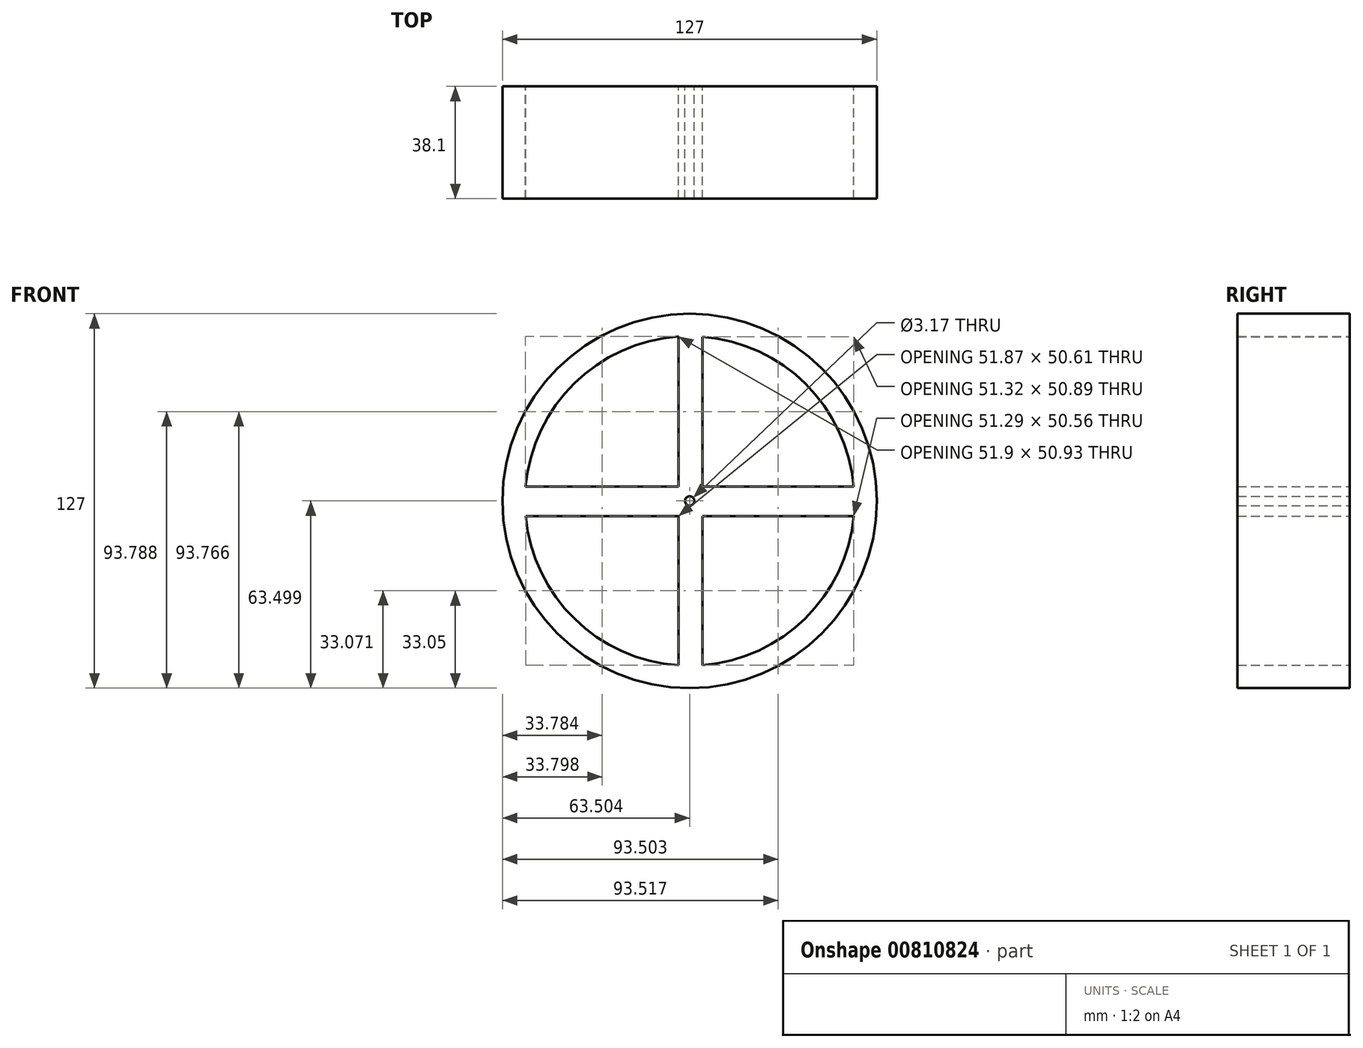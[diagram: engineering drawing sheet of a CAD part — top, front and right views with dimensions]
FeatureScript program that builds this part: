
annotation { "Feature Type Name" : "Feature", "Feature Type Description" : "" }
export const myFeature = defineFeature(function(context is Context, id is Id, definition is map)
    precondition{}
    {
        {
            var Q0;
            Q0=qCreatedBy(makeId("Front.planeOp"),FACE);
            var sketch = newSketch(context, id + "F0", { "sketchPlane" : qUnion([Q0])});
            skCircle(sketch, "E0", {"center": v(-16.13, 21.28) * mm, "radius": 63.5 * mm});
            skCircle(sketch, "E1", {"center": v(-16.13, 21.28) * mm, "radius": 1.59 * mm});
            skArc(sketch, "E2", {"start": v(-71.77, 16.13) * mm, "mid": v(-55.15, -18.72) * mm, "end": v(-19.9, -34.47) * mm});
            skLineSegment(sketch, "E3.left", {"start": v(-19.9, 77.03) * mm, "end": v(-19.9, 26.1) * mm});
            skLineSegment(sketch, "E3.right", {"start": v(-11.77, 76.99) * mm, "end": v(-11.77, 26.1) * mm});
            skLineSegment(sketch, "E4.bottom", {"start": v(-71.8, 26.1) * mm, "end": v(-19.9, 26.1) * mm});
            skLineSegment(sketch, "E4.top", {"start": v(-71.77, 16.13) * mm, "end": v(-19.9, 16.13) * mm});
            skPoint(sketch, "E5.orphan", {"position": v(-16.13, 77.16) * mm});
            skPoint(sketch, "E6.orphan", {"position": v(-16.13, -34.6) * mm});
            skLineSegment(sketch, "E7.trimOffspring", {"start": v(-11.77, 16.13) * mm, "end": v(39.52, 16.13) * mm});
            skLineSegment(sketch, "E8.trimOffspring", {"start": v(-11.77, 26.1) * mm, "end": v(39.55, 26.1) * mm});
            skLineSegment(sketch, "E9.trimOffspring", {"start": v(-19.9, 16.13) * mm, "end": v(-19.9, -34.47) * mm});
            skLineSegment(sketch, "E10.trimOffspring", {"start": v(-11.77, 16.13) * mm, "end": v(-11.77, -34.43) * mm});
            skArc(sketch, "E11.trimOffspring", {"start": v(-19.9, 77.03) * mm, "mid": v(-55.26, 61.16) * mm, "end": v(-71.8, 26.1) * mm});
            skArc(sketch, "E12.trimOffspring", {"start": v(-11.77, -34.43) * mm, "mid": v(23.1, -18.51) * mm, "end": v(39.52, 16.13) * mm});
            skArc(sketch, "E13.trimOffspring", {"start": v(39.55, 26.1) * mm, "mid": v(23.22, 60.96) * mm, "end": v(-11.77, 76.99) * mm});
            skSolve(sketch);
        }
        {
            var Q0;
            Q0 = qSketchRegion(id + "F0", true);
            extrude(context, id + "F1", {"entities" : qUnion([Q0]), "depth" : 38.1 * mm, "offsetDistance" : 25.4 * mm});
        }
    });
